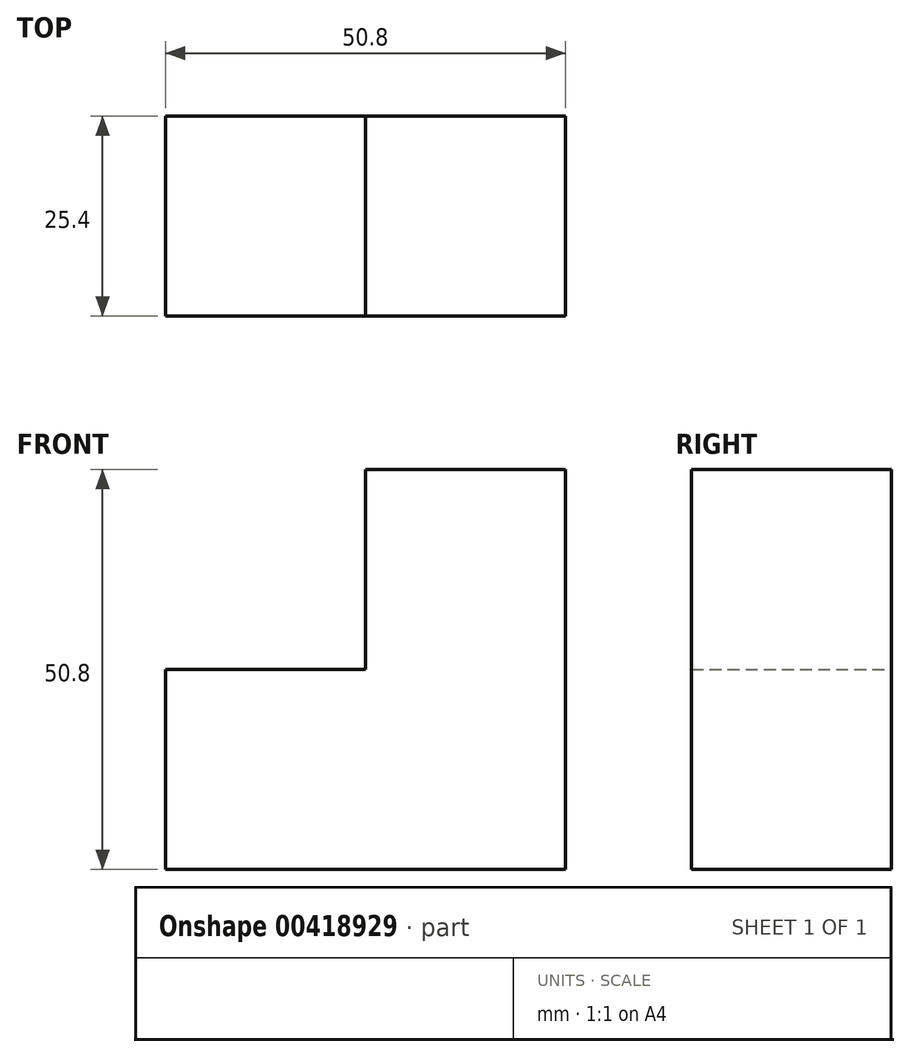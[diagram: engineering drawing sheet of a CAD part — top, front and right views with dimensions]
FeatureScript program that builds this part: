
annotation { "Feature Type Name" : "Feature", "Feature Type Description" : "" }
export const myFeature = defineFeature(function(context is Context, id is Id, definition is map)
    precondition{}
    {
        {
            var Q0;
            Q0=qCreatedBy(makeId("Front.planeOp"),FACE);
            var sketch = newSketch(context, id + "F0", { "sketchPlane" : qUnion([Q0])});
            skLineSegment(sketch, "E0", {"start": v(-50.8, 0) * mm, "end": v(0, 0) * mm});
            skLineSegment(sketch, "E1", {"start": v(0, 0) * mm, "end": v(0, 50.8) * mm});
            skLineSegment(sketch, "E2", {"start": v(0, 50.8) * mm, "end": v(-25.4, 50.8) * mm});
            skLineSegment(sketch, "E3", {"start": v(-25.4, 50.8) * mm, "end": v(-25.4, 25.4) * mm});
            skLineSegment(sketch, "E4", {"start": v(-25.4, 25.4) * mm, "end": v(-50.8, 25.4) * mm});
            skLineSegment(sketch, "E5", {"start": v(-50.8, 25.4) * mm, "end": v(-50.8, 0) * mm});
            skSolve(sketch);
        }
        {
            var Q0;
            Q0 = qSketchRegion(id + "F0", true);
            extrude(context, id + "F1", {"entities" : qUnion([Q0]), "depth" : 25.4 * mm});
        }
    });
